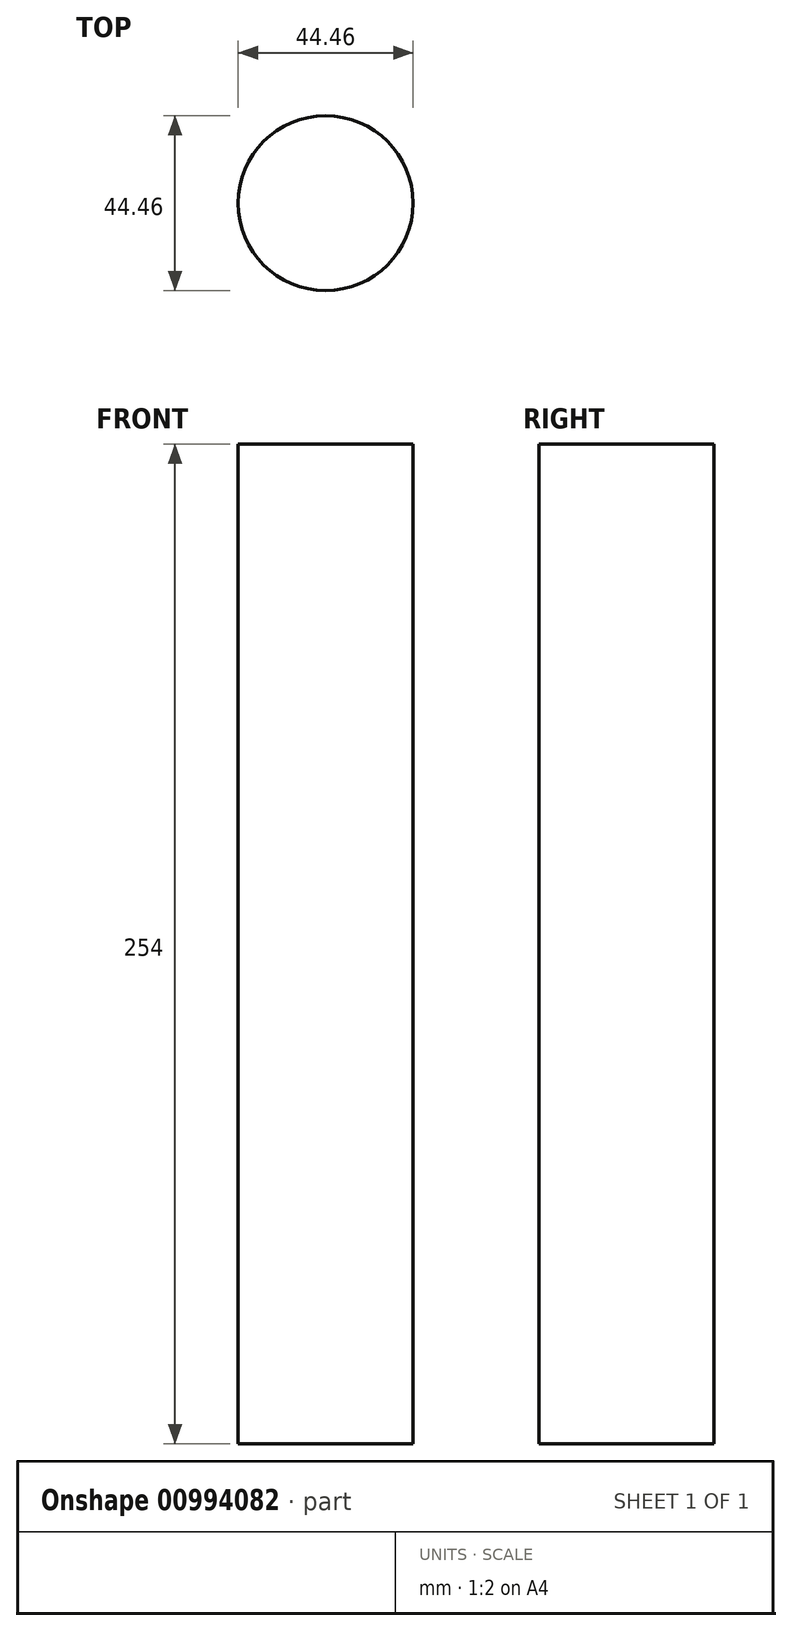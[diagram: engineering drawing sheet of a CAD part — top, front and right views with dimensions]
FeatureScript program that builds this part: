
annotation { "Feature Type Name" : "Feature", "Feature Type Description" : "" }
export const myFeature = defineFeature(function(context is Context, id is Id, definition is map)
    precondition{}
    {
        {
            var Q0;
            Q0=qCreatedBy(makeId("Top.planeOp"),FACE);
            var sketch = newSketch(context, id + "F0", { "sketchPlane" : qUnion([Q0])});
            skCircle(sketch, "E0", {"center": v(0, 0) * mm, "radius": 22.23 * mm});
            skSolve(sketch);
        }
        {
            var Q0;
            Q0 = qSketchRegion(id + "F0", true);
            extrude(context, id + "F1", {"entities" : qUnion([Q0]), "depth" : 254 * mm, "offsetDistance" : 25.4 * mm});
        }
    });
